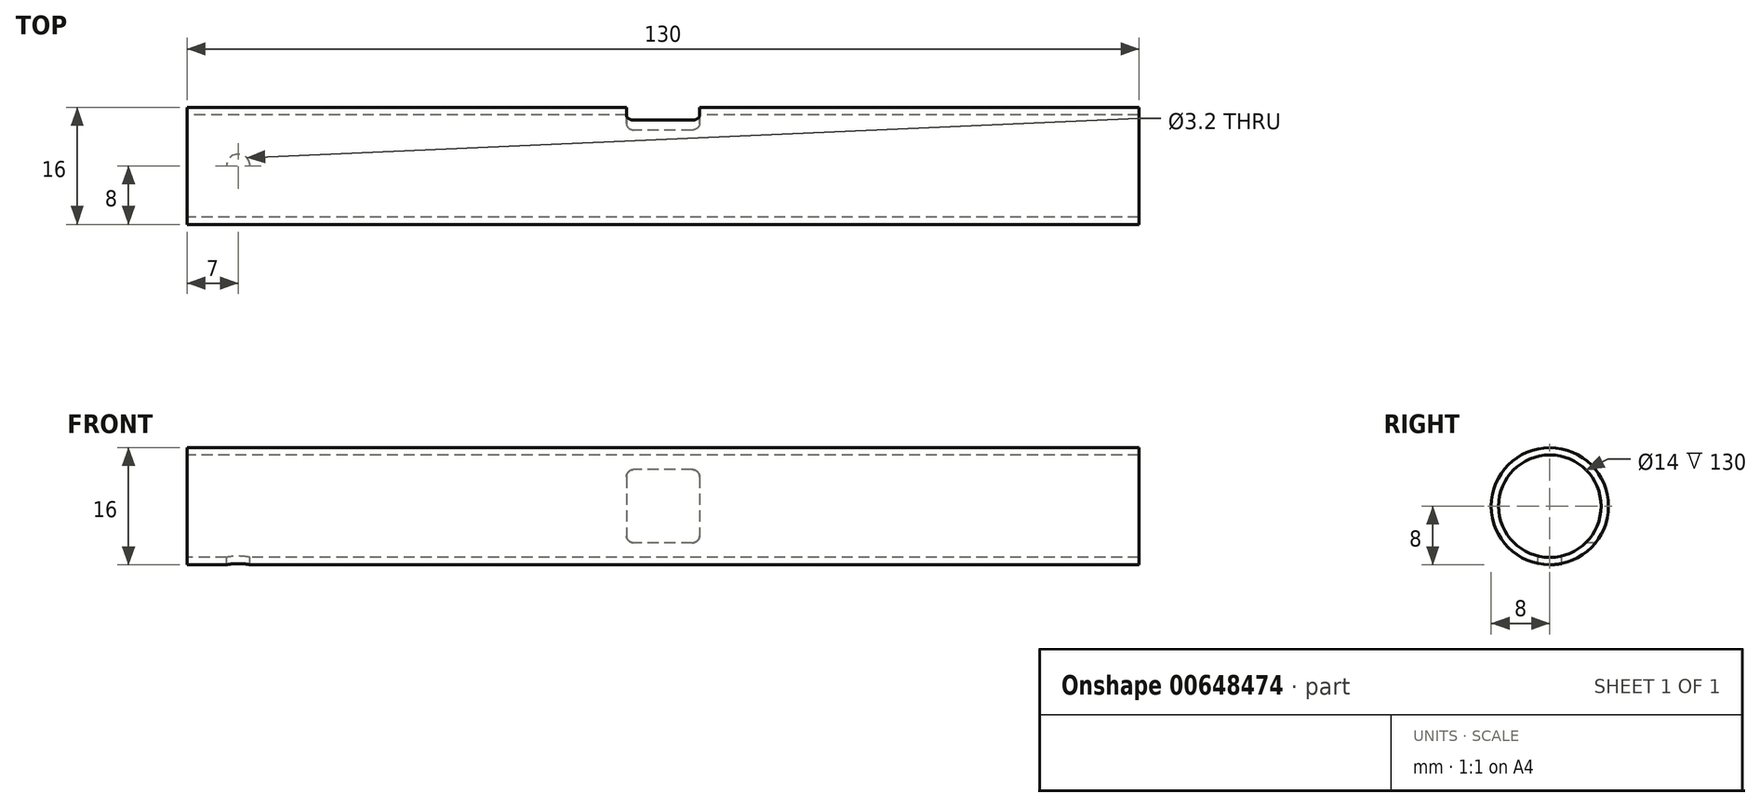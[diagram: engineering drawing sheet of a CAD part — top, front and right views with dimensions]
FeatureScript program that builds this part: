
annotation { "Feature Type Name" : "Feature", "Feature Type Description" : "" }
export const myFeature = defineFeature(function(context is Context, id is Id, definition is map)
    precondition{}
    {
        {
            var Q0;
            Q0=qCreatedBy(makeId("Right.planeOp"),FACE);
            var sketch = newSketch(context, id + "F0", { "sketchPlane" : qUnion([Q0])});
            skCircle(sketch, "E0", {"center": v(0, 0) * mm, "radius": 7 * mm});
            skCircle(sketch, "E1", {"center": v(0, 0) * mm, "radius": 8 * mm});
            skSolve(sketch);
        }
        {
            var Q0;
            Q0 = qSketchRegion(id + "F0", true);
            extrude(context, id + "F1", {"entities" : qUnion([Q0]), "depth" : 130 * mm, "offsetDistance" : 25 * mm, "symmetric" : true});
        }
        {
            var Q0;
            Q0=qCreatedBy(makeId("Front.planeOp"),FACE);
            var sketch = newSketch(context, id + "F2", { "sketchPlane" : qUnion([Q0])});
            skLineSegment(sketch, "E2.bottom", {"start": v(5, 5) * mm, "end": v(-5, 5) * mm});
            skLineSegment(sketch, "E2.top", {"start": v(5, -5) * mm, "end": v(-5, -5) * mm});
            skLineSegment(sketch, "E2.left", {"start": v(5, 5) * mm, "end": v(5, -5) * mm});
            skLineSegment(sketch, "E2.right", {"start": v(-5, 5) * mm, "end": v(-5, -5) * mm});
            skPoint(sketch, "E2.middle", {"position": v(0, 0) * mm});
            skSolve(sketch);
        }
        {
            var Q0;
            Q0 = qSketchRegion(id + "F2", true);
            extrude(context, id + "F3", {"entities" : qUnion([Q0]), "operationType" : NewBodyOperationType.REMOVE, "oppositeDirection" : true, "depth" : 25 * mm, "offsetDistance" : 25 * mm});
        }
        {
            var Q0;
            Q0=makeQuery(id+"F3.boolean.opBoolean","COPY",EDGE,{"derivedFrom":makeQuery(id+"F3.opExtrude","SWEPT_EDGE",EDGE,{"disambiguationData":[OSD([sQuery(id+"F2.wireOp",EDGE,"E2.top"),sQuery(id+"F2.wireOp",EDGE,"E2.right")])]})});
            var Q1;
            Q1=makeQuery(id+"F3.boolean.opBoolean","COPY",EDGE,{"derivedFrom":makeQuery(id+"F3.opExtrude","SWEPT_EDGE",EDGE,{"disambiguationData":[OSD([sQuery(id+"F2.wireOp",EDGE,"E2.top"),sQuery(id+"F2.wireOp",EDGE,"E2.left")])]})});
            var Q2;
            Q2=makeQuery(id+"F3.boolean.opBoolean","COPY",EDGE,{"derivedFrom":makeQuery(id+"F3.opExtrude","SWEPT_EDGE",EDGE,{"disambiguationData":[OSD([sQuery(id+"F2.wireOp",EDGE,"E2.bottom"),sQuery(id+"F2.wireOp",EDGE,"E2.left")])]})});
            var Q3;
            Q3=makeQuery(id+"F3.boolean.opBoolean","COPY",EDGE,{"derivedFrom":makeQuery(id+"F3.opExtrude","SWEPT_EDGE",EDGE,{"disambiguationData":[OSD([sQuery(id+"F2.wireOp",EDGE,"E2.bottom"),sQuery(id+"F2.wireOp",EDGE,"E2.right")])]})});
            fillet(context, id + "F4", {"entities" : qUnion([Q0, Q1, Q2, Q3]), "radius" : 1 * mm, "tangentPropagation" : true, "allowEdgeOverflow" : false});
        }
        {
            var Q0;
            Q0=qCreatedBy(makeId("Top.planeOp"),FACE);
            var sketch = newSketch(context, id + "F5", { "sketchPlane" : qUnion([Q0])});
            skCircle(sketch, "E3", {"center": v(-58, 0) * mm, "radius": 1.6 * mm});
            skSolve(sketch);
        }
        {
            var Q0;
            Q0 = qSketchRegion(id + "F5", true);
            extrude(context, id + "F6", {"entities" : qUnion([Q0]), "operationType" : NewBodyOperationType.REMOVE, "oppositeDirection" : true, "depth" : 25 * mm, "offsetDistance" : 25 * mm});
        }
    });
